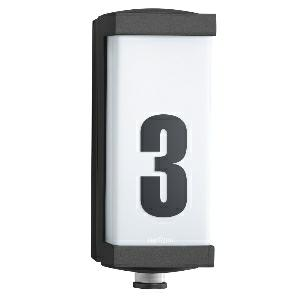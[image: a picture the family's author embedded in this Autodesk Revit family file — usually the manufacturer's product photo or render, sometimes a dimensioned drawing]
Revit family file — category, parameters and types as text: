
# Revit family: l_666_led_053116
name_source: partatom
category: Leuchten
revit_build: Autodesk Revit 2016 (Build: 20190508_0715(x64)
units: mm (PartAtom-declared; Revit-internal decimal feet)

## family parameters
Basisbauteil = Fläche
Beim Laden mit Abzugskörper schneiden = Nein
Bemaßung runder Anschluss = Durchmesser verwenden
Gemeinsam genutzt = Nein
Lichtquelle = Nein
Raumberechnungspunkt = Nein
Teiletyp = Normal

## types (1)
- L 666 LED (1 x , 595 lm, 3000 K)
    Beschreibung = Dimensions (L x W x H): 122 x 102 x 269 mm; Mains power supply: 220 – 240 V / 50 – 60 Hz; Mounting height max.: 2,50 m; Sensor Technology: passive infrared; Output: 9 W; Interconnection: Yes; Slave modeselectable: No; Luminous flux: 595 lm; Efficiency: 66 lm/W; Colour temperature: 3000 K; Colour variation LED: SDCM3; Colour Rendering Index CRI: 80-89; With lamp: Yes, STEINEL LED system; Lamp: LED cannot be replaced; LED life expectancy (max. °C): 50000 h; Base: without; LED cooling system: Passive Thermo Control; With motion detector: Yes; Detection angle: 360 °; Sneak-by guard: Yes; Capability of masking out individual segments: Yes; Electronic scalability: No; Mechanical scalability: No; Reach, radial: r = 2 m (13 m²); Reach, tangential: r = 7 m (154 m²); Photo-cell controller: Yes; Twilight setting: 2 – 2000 lx; Time setting: 5 sec – 15 min; Basic light level function: Yes; Basic light level function time: 10/30 min, all night; Functions: 4 programme settings geared to practical needs, can be selected on removable sensor module; Soft light start: Yes; Continuous light: selectable, 4h; Impact resistance: IK07; IP-rating: IP44; Protection class: I; Ambient temperature: -20 – 50 °C; Housing material: Aluminium; Cover material: Plastic, opal; Manufacturer's Warranty: 5 years; Settings via: Potentiometers; Cover material: shrouds; Version: Anthracite; PU1, EAN: 4007841053116
    Color Rendering = 80-89
    Color Temperature = 3000 K
    Frequency = 50 Hz, 60 Hz
    Height = 269 mm
    Hersteller = Steinel
    Lamp Light Flux = 595 lm
    Lamp count = 1
    Lampe = 1 x
    Length = 122 mm
    Luminous efficacy = 0 lm/W
    ModVariant = Nein
    Modell = 053116
    Mounting Type = Surface mounted
    Number of Poles = 1
    OnlyDefault = Ja
    Power Factor = 1
    Product Name = L 666 LED
    Product group = Sensor-switched indoor light
    ProductGroupID = 30
    Protection Class = Protection class I
    Protection Degree = IP 34
    RlxData = <blob elided: 29609 chars, md5=878e75ff>
    Scheinlast = 9 VA
    Socket = socket
    Standby Power = 0 W
    System Light Flux = 0 lm
    System Power = 9 W
    Typenbild = produkt1_053116.jpg
    Typenkommentare = Product without accessories
    URL = http://relux.com
    VarID = ---
    Voltage = 0 V
    Vorgabe-Ansicht = 1800 mm
    Weight = 0.00 kg
    Width = 102 mm

## geometry (parser evidence)
native form markers: Blend x4, Sweep x6
no freeform markers — native parametric forms only
